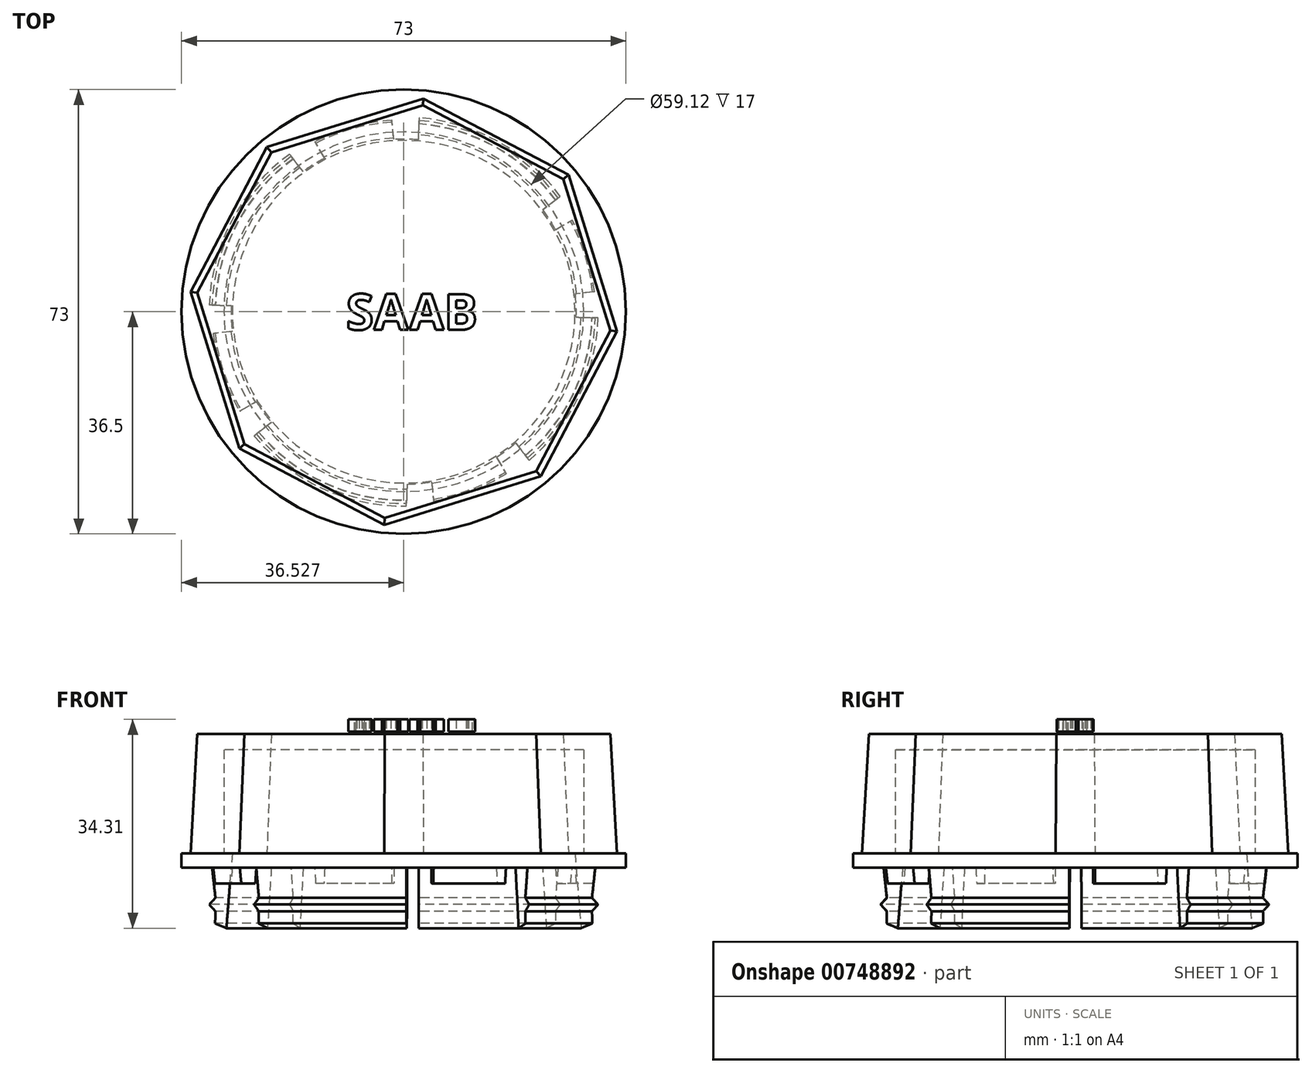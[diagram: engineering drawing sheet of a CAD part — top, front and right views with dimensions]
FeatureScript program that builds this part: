
annotation { "Feature Type Name" : "Feature", "Feature Type Description" : "" }
export const myFeature = defineFeature(function(context is Context, id is Id, definition is map)
    precondition{}
    {
        {
            var Q0;
            Q0=qCreatedBy(makeId("Top.planeOp"),FACE);
            var sketch = newSketch(context, id + "F0", { "sketchPlane" : qUnion([Q0])});
            skCircle(sketch, "E0.cCircle", {"center": v(41.88, 0) * mm, "radius": 35.18 * mm, "construction": true});
            skLineSegment(sketch, "E0.0", {"start": v(14.82, -22.49) * mm, "end": v(6.85, 3.23) * mm});
            skLineSegment(sketch, "E0.1", {"start": v(6.85, 3.23) * mm, "end": v(19.39, 27.05) * mm});
            skLineSegment(sketch, "E0.2", {"start": v(19.39, 27.05) * mm, "end": v(45.1, 35.03) * mm});
            skLineSegment(sketch, "E0.3", {"start": v(45.1, 35.03) * mm, "end": v(68.93, 22.49) * mm});
            skLineSegment(sketch, "E0.4", {"start": v(68.93, 22.49) * mm, "end": v(76.9, -3.23) * mm});
            skLineSegment(sketch, "E0.5", {"start": v(76.9, -3.23) * mm, "end": v(64.36, -27.05) * mm});
            skLineSegment(sketch, "E0.6", {"start": v(64.36, -27.05) * mm, "end": v(38.65, -35.03) * mm});
            skLineSegment(sketch, "E0.7", {"start": v(38.65, -35.03) * mm, "end": v(14.82, -22.49) * mm});
            skSolve(sketch);
        }
        {
            var Q0;
            Q0=qSketchRegion(id+"F0",true);
            extrude(context, id + "F1", {"entities" : qUnion([Q0]), "depth" : 19.6 * mm, "offsetDistance" : 25 * mm, "hasDraft" : true, "draftAngle" : 3 * degree, "draftPullDirection" : true});
        }
        {
            var Q0;
            Q0=qCreatedBy(makeId("Front.planeOp"),FACE);
            var sketch = newSketch(context, id + "F2", { "sketchPlane" : qUnion([Q0])});
            skLineSegment(sketch, "E1", {"start": v(71.3, 19.61) * mm, "end": v(71.3, 20.31) * mm});
            skLineSegment(sketch, "E2", {"start": v(71.3, 20.31) * mm, "end": v(70.7, 20.31) * mm});
            skLineSegment(sketch, "E3", {"start": v(70.7, 20.31) * mm, "end": v(70.7, 19.61) * mm});
            skLineSegment(sketch, "E4", {"start": v(61.4, 22) * mm, "end": v(61.4, 21.36) * mm});
            skLineSegment(sketch, "E5", {"start": v(61.4, 21.36) * mm, "end": v(41.94, 21.36) * mm});
            skArc(sketch, "E6", {"start": v(70.7, 19.61) * mm, "mid": v(66.19, 21.38) * mm, "end": v(61.4, 22) * mm});
            skLineSegment(sketch, "E7", {"start": v(41.94, 21.36) * mm, "end": v(41.94, 19.6) * mm});
            skSolve(sketch);
        }
        {
            var Q0;
            Q0=qSketchRegion(id+"F2",true);
            var Q1;
            Q1=sQuery(id+"F2.wireOp",EDGE,"E5");
            var Q2;
            Q2=sQuery(id+"F2.wireOp",EDGE,"E4");
            var Q3;
            Q3=sQuery(id+"F2.wireOp",EDGE,"E6");
            var Q4;
            Q4=sQuery(id+"F2.wireOp",EDGE,"E1");
            var Q5;
            Q5=sQuery(id+"F2.wireOp",EDGE,"E3");
            var Q6;
            Q6=sQuery(id+"F2.wireOp",EDGE,"E2");
            var Q7;
            Q7=sQuery(id+"F2.wireOp",EDGE,"E7");
            revolve(context, id + "F3", {"bodyType" : ToolBodyType.SURFACE, "surfaceOperationType" : NewSurfaceOperationType.NEW, "entities" : qUnion([Q0]), "surfaceEntities" : qUnion([Q1, Q2, Q3, Q4, Q5, Q6]), "axis" : qUnion([Q7]), "revolveType" : RevolveType.FULL});
        }
        {
            var Q0;
            Q0=qCreatedBy(makeId("Front.planeOp"),FACE);
            var sketch = newSketch(context, id + "F4", { "sketchPlane" : qUnion([Q0])});
            skLineSegment(sketch, "E8", {"start": v(41.85, 2.47) * mm, "end": v(41.85, -0.28) * mm});
            skLineSegment(sketch, "E9", {"start": v(13.92, 0) * mm, "end": v(10.66, 0) * mm});
            skLineSegment(sketch, "E10", {"start": v(13.7, 0) * mm, "end": v(12.7, -12.3) * mm});
            skLineSegment(sketch, "E11", {"start": v(12.7, -12.3) * mm, "end": v(10.85, -11.54) * mm});
            skLineSegment(sketch, "E12", {"start": v(10.85, -11.54) * mm, "end": v(10.9, -9.54) * mm});
            skLineSegment(sketch, "E13", {"start": v(9.9, -8.43) * mm, "end": v(10.9, -9.54) * mm});
            skLineSegment(sketch, "E14", {"start": v(9.9, -8.43) * mm, "end": v(10.9, -7.32) * mm});
            skLineSegment(sketch, "E15", {"start": v(10.9, -7.32) * mm, "end": v(10.35, -2.35) * mm});
            skLineSegment(sketch, "E16", {"start": v(41.85, 0) * mm, "end": v(5.35, 0) * mm});
            skLineSegment(sketch, "E17", {"start": v(41.85, 2.47) * mm, "end": v(41.85, -22.81) * mm});
            skPoint(sketch, "E18", {"position": v(5.35, -2.35) * mm});
            skLineSegment(sketch, "E19", {"start": v(5.35, -2.35) * mm, "end": v(10.35, -2.35) * mm});
            skLineSegment(sketch, "E20", {"start": v(5.35, 0) * mm, "end": v(5.35, -2.35) * mm});
            skPoint(sketch, "E21", {"position": v(10.85, 0) * mm});
            skSolve(sketch);
        }
        {
            var Q0;
            Q0=qSketchRegion(id+"F4",true);
            var Q1;
            Q1=sQuery(id+"F4.wireOp",EDGE,"E16");
            var Q2;
            Q2=sQuery(id+"F4.wireOp",EDGE,"4cd7ZZWE-5ar5-vtm7-FDXw-HXyrbe5Stu3w");
            var Q3;
            Q3=sQuery(id+"F4.wireOp",EDGE,"E15");
            var Q4;
            Q4=sQuery(id+"F4.wireOp",EDGE,"E14");
            var Q5;
            Q5=sQuery(id+"F4.wireOp",EDGE,"E13");
            var Q6;
            Q6=sQuery(id+"F4.wireOp",EDGE,"E11");
            var Q7;
            Q7=sQuery(id+"F4.wireOp",EDGE,"E12");
            var Q8;
            Q8=sQuery(id+"F4.wireOp",EDGE,"E10");
            var Q9;
            Q9=sQuery(id+"F4.wireOp",EDGE,"E17");
            revolve(context, id + "F5", {"surfaceOperationType" : NewSurfaceOperationType.NEW, "entities" : qUnion([Q0]), "surfaceEntities" : qUnion([Q1, Q2, Q3, Q4, Q5, Q6, Q7, Q8]), "axis" : qUnion([Q9]), "revolveType" : RevolveType.FULL});
        }
        {
            var Q0;
            Q0=qCreatedBy(makeId("Top.planeOp"),FACE);
            var sketch = newSketch(context, id + "F6", { "sketchPlane" : qUnion([Q0])});
            skCircle(sketch, "E22", {"center": v(41.88, 0) * mm, "radius": 29.56 * mm});
            skSolve(sketch);
        }
        {
            var Q0;
            Q0=qSketchRegion(id+"F6",true);
            extrude(context, id + "F7", {"entities" : qUnion([Q0]), "operationType" : NewBodyOperationType.REMOVE, "depth" : 17 * mm, "offsetDistance" : 25 * mm});
        }
        {
            var Q0;
            Q0=qCreatedBy(makeId("Top.planeOp"),FACE);
            var sketch = newSketch(context, id + "F8", { "sketchPlane" : qUnion([Q0])});
            skText(sketch, "E23", { "text": "SAAB", "fontName": "OpenSans-Bold.ttf"});
            const initialGuessF8  = {"E23": [0.03239, -0.00298, 1, 0, 0.00593]};
            skSetInitialGuess(sketch, initialGuessF8);
            skSolve(sketch);
        }
        {
            var Q0;
            Q0=qSketchRegion(id+"F8",true);
            extrude(context, id + "F9", {"entities" : qUnion([Q0]), "depth" : 2 * mm, "offsetDistance" : 25 * mm});
        }
        {
            var Q0;
            Q0=makeQuery(id+"F9.opExtrude","SWEPT_BODY",BODY,{"disambiguationData":[OSD([sQuery(id+"F8.wireOp",EDGE,"E23.sketch_text.stroke-0"),sQuery(id+"F8.wireOp",EDGE,"E23.sketch_text.stroke-1"),sQuery(id+"F8.wireOp",EDGE,"E23.sketch_text.stroke-2"),sQuery(id+"F8.wireOp",EDGE,"E23.sketch_text.stroke-3"),sQuery(id+"F8.wireOp",EDGE,"E23.sketch_text.stroke-4"),sQuery(id+"F8.wireOp",EDGE,"E23.sketch_text.stroke-5"),sQuery(id+"F8.wireOp",EDGE,"E23.sketch_text.stroke-6"),sQuery(id+"F8.wireOp",EDGE,"E23.sketch_text.stroke-7"),sQuery(id+"F8.wireOp",EDGE,"E23.sketch_text.stroke-8"),sQuery(id+"F8.wireOp",EDGE,"E23.sketch_text.stroke-9"),sQuery(id+"F8.wireOp",EDGE,"E23.sketch_text.stroke-10"),sQuery(id+"F8.wireOp",EDGE,"E23.sketch_text.stroke-11"),sQuery(id+"F8.wireOp",EDGE,"E23.sketch_text.stroke-12"),sQuery(id+"F8.wireOp",EDGE,"E23.sketch_text.stroke-13"),sQuery(id+"F8.wireOp",EDGE,"E23.sketch_text.stroke-14"),sQuery(id+"F8.wireOp",EDGE,"E23.sketch_text.stroke-15"),sQuery(id+"F8.wireOp",EDGE,"E23.sketch_text.stroke-16"),sQuery(id+"F8.wireOp",EDGE,"E23.sketch_text.stroke-17"),sQuery(id+"F8.wireOp",EDGE,"E23.sketch_text.stroke-18"),sQuery(id+"F8.wireOp",EDGE,"E23.sketch_text.stroke-19"),sQuery(id+"F8.wireOp",EDGE,"E23.sketch_text.stroke-20"),sQuery(id+"F8.wireOp",EDGE,"E23.sketch_text.stroke-21"),sQuery(id+"F8.wireOp",EDGE,"E23.sketch_text.stroke-22"),sQuery(id+"F8.wireOp",EDGE,"E23.sketch_text.stroke-23"),sQuery(id+"F8.wireOp",EDGE,"E23.sketch_text.stroke-24"),sQuery(id+"F8.wireOp",EDGE,"E23.sketch_text.stroke-25"),sQuery(id+"F8.wireOp",EDGE,"E23.sketch_text.stroke-26"),sQuery(id+"F8.wireOp",EDGE,"E23.sketch_text.stroke-27")])]});
            var Q1;
            Q1=makeQuery(id+"F9.opExtrude","SWEPT_BODY",BODY,{"disambiguationData":[OSD([sQuery(id+"F8.wireOp",EDGE,"E23.sketch_text.stroke-28"),sQuery(id+"F8.wireOp",EDGE,"E23.sketch_text.stroke-29"),sQuery(id+"F8.wireOp",EDGE,"E23.sketch_text.stroke-30"),sQuery(id+"F8.wireOp",EDGE,"E23.sketch_text.stroke-31"),sQuery(id+"F8.wireOp",EDGE,"E23.sketch_text.stroke-32"),sQuery(id+"F8.wireOp",EDGE,"E23.sketch_text.stroke-33"),sQuery(id+"F8.wireOp",EDGE,"E23.sketch_text.stroke-34"),sQuery(id+"F8.wireOp",EDGE,"E23.sketch_text.stroke-35"),sQuery(id+"F8.wireOp",EDGE,"E23.sketch_text.stroke-36"),sQuery(id+"F8.wireOp",EDGE,"E23.sketch_text.stroke-37"),sQuery(id+"F8.wireOp",EDGE,"E23.sketch_text.stroke-38"),sQuery(id+"F8.wireOp",EDGE,"E23.sketch_text.stroke-39")])]});
            var Q2;
            Q2=makeQuery(id+"F9.opExtrude","SWEPT_BODY",BODY,{"disambiguationData":[OSD([sQuery(id+"F8.wireOp",EDGE,"E23.sketch_text.stroke-40"),sQuery(id+"F8.wireOp",EDGE,"E23.sketch_text.stroke-41"),sQuery(id+"F8.wireOp",EDGE,"E23.sketch_text.stroke-42"),sQuery(id+"F8.wireOp",EDGE,"E23.sketch_text.stroke-43"),sQuery(id+"F8.wireOp",EDGE,"E23.sketch_text.stroke-44"),sQuery(id+"F8.wireOp",EDGE,"E23.sketch_text.stroke-45"),sQuery(id+"F8.wireOp",EDGE,"E23.sketch_text.stroke-46"),sQuery(id+"F8.wireOp",EDGE,"E23.sketch_text.stroke-47"),sQuery(id+"F8.wireOp",EDGE,"E23.sketch_text.stroke-48"),sQuery(id+"F8.wireOp",EDGE,"E23.sketch_text.stroke-49"),sQuery(id+"F8.wireOp",EDGE,"E23.sketch_text.stroke-50"),sQuery(id+"F8.wireOp",EDGE,"E23.sketch_text.stroke-51")])]});
            var Q3;
            Q3=makeQuery(id+"F9.opExtrude","SWEPT_BODY",BODY,{"disambiguationData":[OSD([sQuery(id+"F8.wireOp",EDGE,"E23.sketch_text.stroke-52"),sQuery(id+"F8.wireOp",EDGE,"E23.sketch_text.stroke-53"),sQuery(id+"F8.wireOp",EDGE,"E23.sketch_text.stroke-54"),sQuery(id+"F8.wireOp",EDGE,"E23.sketch_text.stroke-55"),sQuery(id+"F8.wireOp",EDGE,"E23.sketch_text.stroke-56"),sQuery(id+"F8.wireOp",EDGE,"E23.sketch_text.stroke-57"),sQuery(id+"F8.wireOp",EDGE,"E23.sketch_text.stroke-58"),sQuery(id+"F8.wireOp",EDGE,"E23.sketch_text.stroke-59"),sQuery(id+"F8.wireOp",EDGE,"E23.sketch_text.stroke-60"),sQuery(id+"F8.wireOp",EDGE,"E23.sketch_text.stroke-61"),sQuery(id+"F8.wireOp",EDGE,"E23.sketch_text.stroke-62"),sQuery(id+"F8.wireOp",EDGE,"E23.sketch_text.stroke-63"),sQuery(id+"F8.wireOp",EDGE,"E23.sketch_text.stroke-64"),sQuery(id+"F8.wireOp",EDGE,"E23.sketch_text.stroke-65"),sQuery(id+"F8.wireOp",EDGE,"E23.sketch_text.stroke-66"),sQuery(id+"F8.wireOp",EDGE,"E23.sketch_text.stroke-67"),sQuery(id+"F8.wireOp",EDGE,"E23.sketch_text.stroke-68"),sQuery(id+"F8.wireOp",EDGE,"E23.sketch_text.stroke-69"),sQuery(id+"F8.wireOp",EDGE,"E23.sketch_text.stroke-70"),sQuery(id+"F8.wireOp",EDGE,"E23.sketch_text.stroke-71"),sQuery(id+"F8.wireOp",EDGE,"E23.sketch_text.stroke-72"),sQuery(id+"F8.wireOp",EDGE,"E23.sketch_text.stroke-73"),sQuery(id+"F8.wireOp",EDGE,"E23.sketch_text.stroke-74"),sQuery(id+"F8.wireOp",EDGE,"E23.sketch_text.stroke-75"),sQuery(id+"F8.wireOp",EDGE,"E23.sketch_text.stroke-76")])]});
            transform(context, id + "F10", {"entities" : qUnion([Q0, Q1, Q2, Q3]), "transformType" : TransformType.TRANSLATION_3D, "dx" : 0 * mm, "dy" : 0 * mm, "dz" : 20 * mm, "makeCopy" : false});
        }
        {
            var Q0;
            Q0=qCreatedBy(makeId("Top.planeOp"),FACE);
            var sketch = newSketch(context, id + "F11", { "sketchPlane" : qUnion([Q0])});
            skLineSegment(sketch, "E24", {"start": v(69.85, -34.13) * mm, "end": v(16.32, 34.78) * mm});
            skLineSegment(sketch, "E25", {"start": v(16.32, 34.78) * mm, "end": v(43.91, 43.26) * mm});
            skLineSegment(sketch, "E26", {"start": v(43.91, 43.26) * mm, "end": v(42.61, -43.16) * mm});
            skLineSegment(sketch, "E27", {"start": v(9.14, -26.59) * mm, "end": v(79.03, 27.7) * mm});
            skLineSegment(sketch, "E28", {"start": v(79.03, 27.7) * mm, "end": v(86.57, -0.61) * mm});
            skLineSegment(sketch, "E29", {"start": v(86.57, -0.61) * mm, "end": v(43.22, 0) * mm});
            skLineSegment(sketch, "E30", {"start": v(42.61, -43.16) * mm, "end": v(69.85, -34.13) * mm});
            skLineSegment(sketch, "E31", {"start": v(0, 0.68) * mm, "end": v(43.22, 0) * mm});
            skLineSegment(sketch, "E32", {"start": v(9.14, -26.59) * mm, "end": v(0, 0.68) * mm});
            skPoint(sketch, "E33", {"position": v(19.48, -18.55) * mm});
            skPoint(sketch, "E34", {"position": v(12.6, 0.48) * mm});
            skPoint(sketch, "E35", {"position": v(24.83, 23.83) * mm});
            skPoint(sketch, "E36", {"position": v(42.83, -28.88) * mm});
            skPoint(sketch, "E37", {"position": v(60.43, -22) * mm});
            skPoint(sketch, "E38", {"position": v(71.17, -0.4) * mm});
            skPoint(sketch, "E39", {"position": v(65.22, 16.98) * mm});
            skPoint(sketch, "E40", {"position": v(43.69, 28.4) * mm});
            skLineSegment(sketch, "E41", {"start": v(12.6, 0.48) * mm, "end": v(19.48, -18.55) * mm});
            skLineSegment(sketch, "E42", {"start": v(24.83, 23.83) * mm, "end": v(43.69, 28.4) * mm});
            skLineSegment(sketch, "E43", {"start": v(65.22, 16.98) * mm, "end": v(71.17, -0.4) * mm});
            skLineSegment(sketch, "E44", {"start": v(60.43, -22) * mm, "end": v(42.83, -28.88) * mm});
            skSolve(sketch);
        }
        {
            var Q0;
            Q0=qSketchRegion(id+"F11",true);
            extrude(context, id + "F12", {"entities" : qUnion([Q0]), "oppositeDirection" : true, "depth" : 25 * mm, "offsetDistance" : 25 * mm, "hasSecondDirection" : true, "secondDirectionOppositeDirection" : true, "secondDirectionDepth" : 5 * mm});
        }
        {
            var Q0;
            Q0=makeQuery(id+"F12.opExtrude","SWEPT_BODY",BODY,{"disambiguationData":[OSD([sQuery(id+"F11.wireOp",EDGE,"E24"),sQuery(id+"F11.wireOp",EDGE,"E26"),sQuery(id+"F11.wireOp",EDGE,"E27"),sQuery(id+"F11.wireOp",EDGE,"E29"),sQuery(id+"F11.wireOp",EDGE,"E30"),sQuery(id+"F11.wireOp",EDGE,"E31"),sQuery(id+"F11.wireOp",EDGE,"E32")])]});
            var Q1;
            Q1=makeQuery(id+"F12.opExtrude","SWEPT_BODY",BODY,{"disambiguationData":[OSD([sQuery(id+"F11.wireOp",EDGE,"E27"),sQuery(id+"F11.wireOp",EDGE,"E28"),sQuery(id+"F11.wireOp",EDGE,"E29")])]});
            var Q2;
            Q2=makeQuery(id+"F12.opExtrude","SWEPT_BODY",BODY,{"disambiguationData":[OSD([sQuery(id+"F11.wireOp",EDGE,"E24"),sQuery(id+"F11.wireOp",EDGE,"E25"),sQuery(id+"F11.wireOp",EDGE,"E26")])]});
            var Q3;
            Q3=makeQuery(id+"FadKjfFnsJpzDV8_9.opBoolean","SPLIT",BODY,{"disambiguationData":[OD(5.0)],"derivedFrom":makeQuery(id+"F5.opRevolve","SWEPT_BODY",BODY,{"disambiguationData":[OSD([sQuery(id+"F4.wireOp",EDGE,"E10"),sQuery(id+"F4.wireOp",EDGE,"E11"),sQuery(id+"F4.wireOp",EDGE,"E12"),sQuery(id+"F4.wireOp",EDGE,"E13"),sQuery(id+"F4.wireOp",EDGE,"E14"),sQuery(id+"F4.wireOp",EDGE,"E15"),sQuery(id+"F4.wireOp",EDGE,"E16"),sQuery(id+"F4.wireOp",EDGE,"E19"),sQuery(id+"F4.wireOp",EDGE,"E20")])]})});
            var Q4;
            Q4=makeQuery(id+"FadKjfFnsJpzDV8_9.opBoolean","SPLIT",BODY,{"disambiguationData":[OD(3.0)],"derivedFrom":makeQuery(id+"F5.opRevolve","SWEPT_BODY",BODY,{"disambiguationData":[OSD([sQuery(id+"F4.wireOp",EDGE,"E10"),sQuery(id+"F4.wireOp",EDGE,"E11"),sQuery(id+"F4.wireOp",EDGE,"E12"),sQuery(id+"F4.wireOp",EDGE,"E13"),sQuery(id+"F4.wireOp",EDGE,"E14"),sQuery(id+"F4.wireOp",EDGE,"E15"),sQuery(id+"F4.wireOp",EDGE,"E16"),sQuery(id+"F4.wireOp",EDGE,"E19"),sQuery(id+"F4.wireOp",EDGE,"E20")])]})});
            var Q5;
            Q5=makeQuery(id+"FadKjfFnsJpzDV8_9.opBoolean","SPLIT",BODY,{"disambiguationData":[OD(7.0)],"derivedFrom":makeQuery(id+"F5.opRevolve","SWEPT_BODY",BODY,{"disambiguationData":[OSD([sQuery(id+"F4.wireOp",EDGE,"E10"),sQuery(id+"F4.wireOp",EDGE,"E11"),sQuery(id+"F4.wireOp",EDGE,"E12"),sQuery(id+"F4.wireOp",EDGE,"E13"),sQuery(id+"F4.wireOp",EDGE,"E14"),sQuery(id+"F4.wireOp",EDGE,"E15"),sQuery(id+"F4.wireOp",EDGE,"E16"),sQuery(id+"F4.wireOp",EDGE,"E19"),sQuery(id+"F4.wireOp",EDGE,"E20")])]})});
            var Q6;
            Q6=makeQuery(id+"FadKjfFnsJpzDV8_9.opBoolean","SPLIT",BODY,{"disambiguationData":[OD(2.0)],"derivedFrom":makeQuery(id+"F5.opRevolve","SWEPT_BODY",BODY,{"disambiguationData":[OSD([sQuery(id+"F4.wireOp",EDGE,"E10"),sQuery(id+"F4.wireOp",EDGE,"E11"),sQuery(id+"F4.wireOp",EDGE,"E12"),sQuery(id+"F4.wireOp",EDGE,"E13"),sQuery(id+"F4.wireOp",EDGE,"E14"),sQuery(id+"F4.wireOp",EDGE,"E15"),sQuery(id+"F4.wireOp",EDGE,"E16"),sQuery(id+"F4.wireOp",EDGE,"E19"),sQuery(id+"F4.wireOp",EDGE,"E20")])]})});
            var Q7;
            Q7=makeQuery(id+"FadKjfFnsJpzDV8_9.opBoolean","SPLIT",BODY,{"disambiguationData":[OD(0.0)],"derivedFrom":makeQuery(id+"F5.opRevolve","SWEPT_BODY",BODY,{"disambiguationData":[OSD([sQuery(id+"F4.wireOp",EDGE,"E10"),sQuery(id+"F4.wireOp",EDGE,"E11"),sQuery(id+"F4.wireOp",EDGE,"E12"),sQuery(id+"F4.wireOp",EDGE,"E13"),sQuery(id+"F4.wireOp",EDGE,"E14"),sQuery(id+"F4.wireOp",EDGE,"E15"),sQuery(id+"F4.wireOp",EDGE,"E16"),sQuery(id+"F4.wireOp",EDGE,"E19"),sQuery(id+"F4.wireOp",EDGE,"E20")])]})});
            var Q8;
            Q8=makeQuery(id+"FadKjfFnsJpzDV8_9.opBoolean","SPLIT",BODY,{"disambiguationData":[OD(6.0)],"derivedFrom":makeQuery(id+"F5.opRevolve","SWEPT_BODY",BODY,{"disambiguationData":[OSD([sQuery(id+"F4.wireOp",EDGE,"E10"),sQuery(id+"F4.wireOp",EDGE,"E11"),sQuery(id+"F4.wireOp",EDGE,"E12"),sQuery(id+"F4.wireOp",EDGE,"E13"),sQuery(id+"F4.wireOp",EDGE,"E14"),sQuery(id+"F4.wireOp",EDGE,"E15"),sQuery(id+"F4.wireOp",EDGE,"E16"),sQuery(id+"F4.wireOp",EDGE,"E19"),sQuery(id+"F4.wireOp",EDGE,"E20")])]})});
            var Q9;
            Q9=makeQuery(id+"FadKjfFnsJpzDV8_9.opBoolean","SPLIT",BODY,{"disambiguationData":[OD(4.0)],"derivedFrom":makeQuery(id+"F5.opRevolve","SWEPT_BODY",BODY,{"disambiguationData":[OSD([sQuery(id+"F4.wireOp",EDGE,"E10"),sQuery(id+"F4.wireOp",EDGE,"E11"),sQuery(id+"F4.wireOp",EDGE,"E12"),sQuery(id+"F4.wireOp",EDGE,"E13"),sQuery(id+"F4.wireOp",EDGE,"E14"),sQuery(id+"F4.wireOp",EDGE,"E15"),sQuery(id+"F4.wireOp",EDGE,"E16"),sQuery(id+"F4.wireOp",EDGE,"E19"),sQuery(id+"F4.wireOp",EDGE,"E20")])]})});
            var Q10;
            Q10=makeQuery(id+"FadKjfFnsJpzDV8_9.opBoolean","SPLIT",BODY,{"disambiguationData":[OD(1.0)],"derivedFrom":makeQuery(id+"F5.opRevolve","SWEPT_BODY",BODY,{"disambiguationData":[OSD([sQuery(id+"F4.wireOp",EDGE,"E10"),sQuery(id+"F4.wireOp",EDGE,"E11"),sQuery(id+"F4.wireOp",EDGE,"E12"),sQuery(id+"F4.wireOp",EDGE,"E13"),sQuery(id+"F4.wireOp",EDGE,"E14"),sQuery(id+"F4.wireOp",EDGE,"E15"),sQuery(id+"F4.wireOp",EDGE,"E16"),sQuery(id+"F4.wireOp",EDGE,"E19"),sQuery(id+"F4.wireOp",EDGE,"E20")])]})});
            booleanBodies(context, id + "F13", {"operationType" : BooleanOperationType.SUBTRACTION, "tools" : qUnion([Q0, Q1, Q2]), "targets" : qUnion([Q3, Q4, Q5, Q6, Q7, Q8, Q9, Q10])});
        }
        {
            var Q0;
            Q0=qCreatedBy(makeId("Top.planeOp"),FACE);
            var sketch = newSketch(context, id + "F14", { "sketchPlane" : qUnion([Q0])});
            skPoint(sketch, "E45.endSnap0", {"position": v(222.12, 4.24) * mm});
            skPoint(sketch, "E46", {"position": v(43.35, 0) * mm});
            skLineSegment(sketch, "E47", {"start": v(76.6, 26.03) * mm, "end": v(5.98, -29.26) * mm});
            skLineSegment(sketch, "E48", {"start": v(43.35, 0) * mm, "end": v(74.1, -39.28) * mm});
            skLineSegment(sketch, "E49", {"start": v(43.35, 0) * mm, "end": v(14.72, 36.58) * mm});
            skLineSegment(sketch, "E50", {"start": v(1.61, -23.99) * mm, "end": v(43.35, 0) * mm});
            skLineSegment(sketch, "E51", {"start": v(43.35, 0) * mm, "end": v(69.77, -45.97) * mm});
            skLineSegment(sketch, "E52", {"start": v(43.35, 0) * mm, "end": v(81.27, 21.79) * mm});
            skLineSegment(sketch, "E53", {"start": v(43.35, 0) * mm, "end": v(20.03, 40.59) * mm});
            skLineSegment(sketch, "E54", {"start": v(14.72, 36.58) * mm, "end": v(20.03, 40.59) * mm});
            skLineSegment(sketch, "E55", {"start": v(76.6, 26.03) * mm, "end": v(81.27, 21.79) * mm});
            skLineSegment(sketch, "E56", {"start": v(74.1, -39.28) * mm, "end": v(69.77, -45.97) * mm});
            skLineSegment(sketch, "E57", {"start": v(5.98, -29.26) * mm, "end": v(1.61, -23.99) * mm});
            skLineSegment(sketch, "E58", {"start": v(85.32, 4.6) * mm, "end": v(-3.82, -5.18) * mm});
            skLineSegment(sketch, "E59", {"start": v(43.35, 0) * mm, "end": v(48.8, -49.6) * mm});
            skLineSegment(sketch, "E60", {"start": v(43.35, 0) * mm, "end": v(38.29, 46.18) * mm});
            skLineSegment(sketch, "E61", {"start": v(-4.76, 1.6) * mm, "end": v(43.35, 0) * mm});
            skLineSegment(sketch, "E62", {"start": v(43.35, 0) * mm, "end": v(41.59, -52.99) * mm});
            skLineSegment(sketch, "E63", {"start": v(43.35, 0) * mm, "end": v(87.06, -1.46) * mm});
            skLineSegment(sketch, "E64", {"start": v(43.35, 0) * mm, "end": v(44.92, 46.79) * mm});
            skLineSegment(sketch, "E65", {"start": v(38.29, 46.18) * mm, "end": v(44.92, 46.79) * mm});
            skLineSegment(sketch, "E66", {"start": v(85.32, 4.6) * mm, "end": v(87.06, -1.46) * mm});
            skLineSegment(sketch, "E67", {"start": v(48.8, -49.6) * mm, "end": v(41.59, -52.99) * mm});
            skLineSegment(sketch, "E68", {"start": v(-3.82, -5.18) * mm, "end": v(-4.76, 1.6) * mm});
            skSolve(sketch);
        }
        {
            var Q0;
            Q0=qSketchRegion(id+"F14",true);
            extrude(context, id + "F15", {"entities" : qUnion([Q0]), "oppositeDirection" : true, "depth" : 10 * mm, "offsetDistance" : 25 * mm});
        }
        {
            var Q0;
            Q0=makeQuery(id+"F15.opExtrude","SWEPT_BODY",BODY,{"disambiguationData":[OSD([sQuery(id+"F14.wireOp",EDGE,"E49"),sQuery(id+"F14.wireOp",EDGE,"E53"),sQuery(id+"F14.wireOp",EDGE,"E54")])]});
            var Q1;
            Q1=makeQuery(id+"F15.opExtrude","SWEPT_BODY",BODY,{"disambiguationData":[OSD([sQuery(id+"F14.wireOp",EDGE,"E58"),sQuery(id+"F14.wireOp",EDGE,"E61"),sQuery(id+"F14.wireOp",EDGE,"E68")])]});
            var Q2;
            Q2=makeQuery(id+"F15.opExtrude","SWEPT_BODY",BODY,{"disambiguationData":[OSD([sQuery(id+"F14.wireOp",EDGE,"E47"),sQuery(id+"F14.wireOp",EDGE,"E50"),sQuery(id+"F14.wireOp",EDGE,"E57")])]});
            var Q3;
            Q3=makeQuery(id+"F15.opExtrude","SWEPT_BODY",BODY,{"disambiguationData":[OSD([sQuery(id+"F14.wireOp",EDGE,"E59"),sQuery(id+"F14.wireOp",EDGE,"E62"),sQuery(id+"F14.wireOp",EDGE,"E67")])]});
            var Q4;
            Q4=makeQuery(id+"F15.opExtrude","SWEPT_BODY",BODY,{"disambiguationData":[OSD([sQuery(id+"F14.wireOp",EDGE,"E48"),sQuery(id+"F14.wireOp",EDGE,"E51"),sQuery(id+"F14.wireOp",EDGE,"E56")])]});
            var Q5;
            Q5=makeQuery(id+"F15.opExtrude","SWEPT_BODY",BODY,{"disambiguationData":[OSD([sQuery(id+"F14.wireOp",EDGE,"E58"),sQuery(id+"F14.wireOp",EDGE,"E63"),sQuery(id+"F14.wireOp",EDGE,"E66")])]});
            var Q6;
            Q6=makeQuery(id+"F15.opExtrude","SWEPT_BODY",BODY,{"disambiguationData":[OSD([sQuery(id+"F14.wireOp",EDGE,"E47"),sQuery(id+"F14.wireOp",EDGE,"E52"),sQuery(id+"F14.wireOp",EDGE,"E55")])]});
            var Q7;
            Q7=makeQuery(id+"F15.opExtrude","SWEPT_BODY",BODY,{"disambiguationData":[OSD([sQuery(id+"F14.wireOp",EDGE,"E60"),sQuery(id+"F14.wireOp",EDGE,"E64"),sQuery(id+"F14.wireOp",EDGE,"E65")])]});
            transform(context, id + "F16", {"entities" : qUnion([Q0, Q1, Q2, Q3, Q4, Q5, Q6, Q7]), "transformType" : TransformType.TRANSLATION_3D, "dx" : 0 * mm, "dy" : 0 * mm, "dz" : -2.35 * mm, "makeCopy" : false});
        }
        {
            var Q0;
            Q0=makeQuery(id+"F15.opExtrude","SWEPT_BODY",BODY,{"disambiguationData":[OSD([sQuery(id+"F14.wireOp",EDGE,"E49"),sQuery(id+"F14.wireOp",EDGE,"E53"),sQuery(id+"F14.wireOp",EDGE,"E54")])]});
            var Q1;
            Q1=makeQuery(id+"F15.opExtrude","SWEPT_BODY",BODY,{"disambiguationData":[OSD([sQuery(id+"F14.wireOp",EDGE,"E58"),sQuery(id+"F14.wireOp",EDGE,"E61"),sQuery(id+"F14.wireOp",EDGE,"E68")])]});
            var Q2;
            Q2=makeQuery(id+"F15.opExtrude","SWEPT_BODY",BODY,{"disambiguationData":[OSD([sQuery(id+"F14.wireOp",EDGE,"E47"),sQuery(id+"F14.wireOp",EDGE,"E50"),sQuery(id+"F14.wireOp",EDGE,"E57")])]});
            var Q3;
            Q3=makeQuery(id+"F15.opExtrude","SWEPT_BODY",BODY,{"disambiguationData":[OSD([sQuery(id+"F14.wireOp",EDGE,"E59"),sQuery(id+"F14.wireOp",EDGE,"E62"),sQuery(id+"F14.wireOp",EDGE,"E67")])]});
            var Q4;
            Q4=makeQuery(id+"F15.opExtrude","SWEPT_BODY",BODY,{"disambiguationData":[OSD([sQuery(id+"F14.wireOp",EDGE,"E48"),sQuery(id+"F14.wireOp",EDGE,"E51"),sQuery(id+"F14.wireOp",EDGE,"E56")])]});
            var Q5;
            Q5=makeQuery(id+"F15.opExtrude","SWEPT_BODY",BODY,{"disambiguationData":[OSD([sQuery(id+"F14.wireOp",EDGE,"E58"),sQuery(id+"F14.wireOp",EDGE,"E63"),sQuery(id+"F14.wireOp",EDGE,"E66")])]});
            var Q6;
            Q6=makeQuery(id+"F15.opExtrude","SWEPT_BODY",BODY,{"disambiguationData":[OSD([sQuery(id+"F14.wireOp",EDGE,"E47"),sQuery(id+"F14.wireOp",EDGE,"E52"),sQuery(id+"F14.wireOp",EDGE,"E55")])]});
            var Q7;
            Q7=makeQuery(id+"F15.opExtrude","SWEPT_BODY",BODY,{"disambiguationData":[OSD([sQuery(id+"F14.wireOp",EDGE,"E60"),sQuery(id+"F14.wireOp",EDGE,"E64"),sQuery(id+"F14.wireOp",EDGE,"E65")])]});
            var Q8;
            Q8=makeQuery(id+"F5.opRevolve","SWEPT_BODY",BODY,{"disambiguationData":[OSD([sQuery(id+"F4.wireOp",EDGE,"E10"),sQuery(id+"F4.wireOp",EDGE,"E11"),sQuery(id+"F4.wireOp",EDGE,"E12"),sQuery(id+"F4.wireOp",EDGE,"E13"),sQuery(id+"F4.wireOp",EDGE,"E14"),sQuery(id+"F4.wireOp",EDGE,"E15"),sQuery(id+"F4.wireOp",EDGE,"E16"),sQuery(id+"F4.wireOp",EDGE,"E19"),sQuery(id+"F4.wireOp",EDGE,"E20")])]});
            booleanBodies(context, id + "F17", {"operationType" : BooleanOperationType.SUBTRACTION, "tools" : qUnion([Q0, Q1, Q2, Q3, Q4, Q5, Q6, Q7]), "targets" : qUnion([Q8])});
        }
    });
